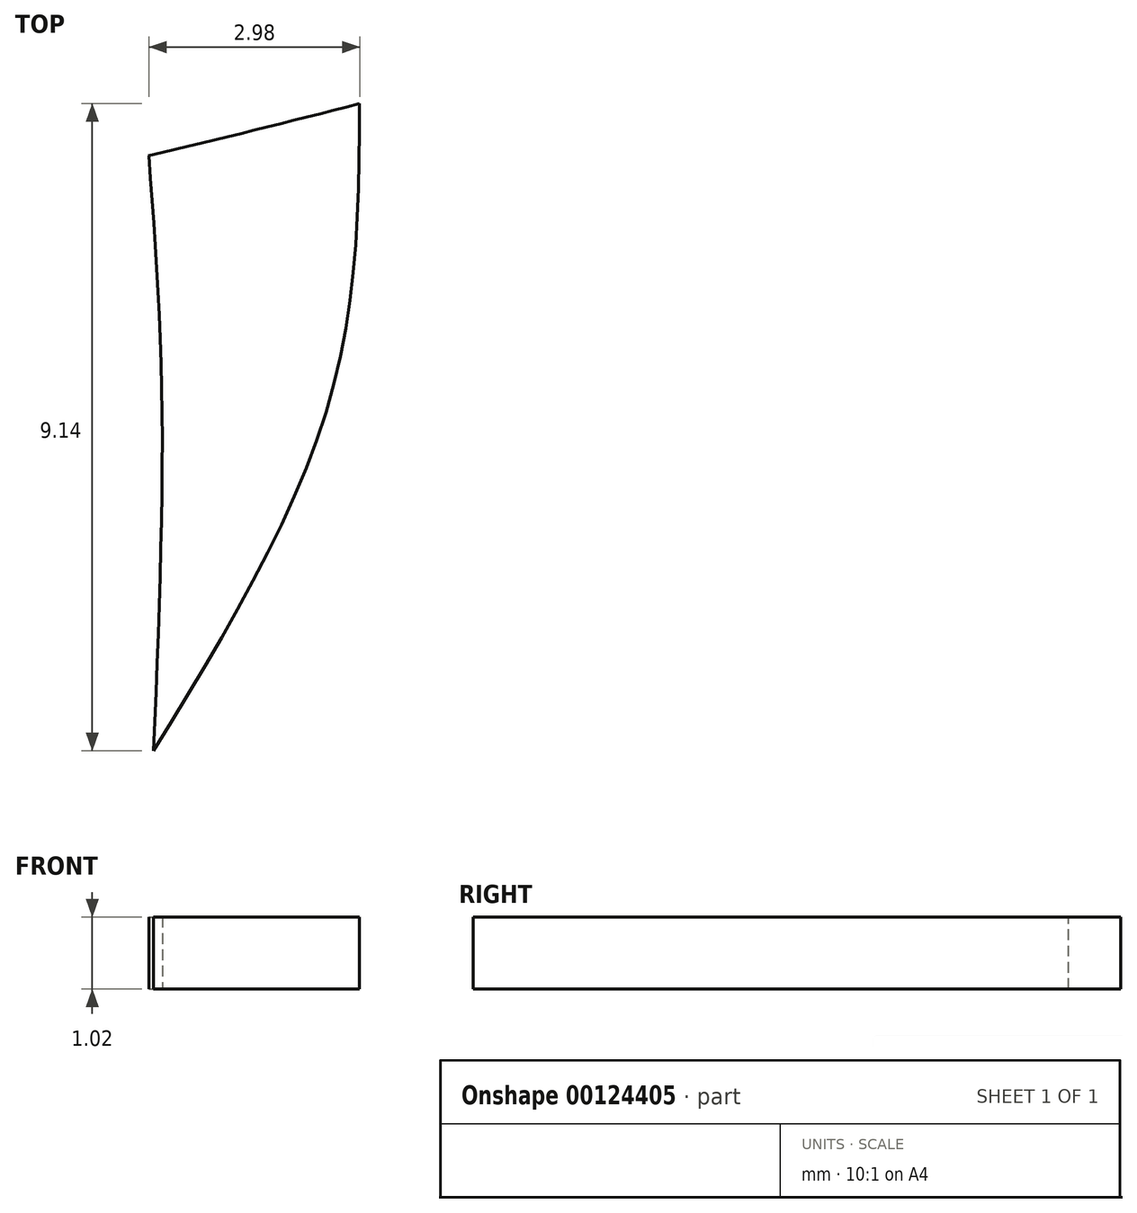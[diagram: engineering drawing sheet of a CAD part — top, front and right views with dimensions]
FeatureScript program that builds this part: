
annotation { "Feature Type Name" : "Feature", "Feature Type Description" : "" }
export const myFeature = defineFeature(function(context is Context, id is Id, definition is map)
    precondition{}
    {
        {
            var Q0;
            Q0=qCreatedBy(makeId("Top.planeOp"),FACE);
            var sketch = newSketch(context, id + "F0", { "sketchPlane" : qUnion([Q0])});
            skCircle(sketch, "E0", {"center": v(-65.84, 32.23) * mm, "radius": 0.65 * mm});
            skSolve(sketch);
        }
        {
            var Q0;
            Q0=qCreatedBy(makeId("Top.planeOp"),FACE);
            var sketch = newSketch(context, id + "F1", { "sketchPlane" : qUnion([Q0])});
            skLineSegment(sketch, "E1", {"start": v(-110.86, 15.85) * mm, "end": v(-22.98, 15.85) * mm});
            skLineSegment(sketch, "E2", {"start": v(-22.98, 15.85) * mm, "end": v(-22.98, -6.27) * mm});
            skLineSegment(sketch, "E3", {"start": v(-110.86, 15.85) * mm, "end": v(-110.86, -6.84) * mm});
            skArc(sketch, "E4", {"start": v(-110.86, -6.84) * mm, "mid": v(-66.88, -13.24) * mm, "end": v(-22.98, -6.27) * mm});
            skFitSpline(sketch, "E5", {"points": [v(-30.88, -8.55) * mm, v(-31.34, -12.85) * mm, v(-33.8, -17.7) * mm], "startDerivative": vector(-0.02, -9.29) * mm, "endDerivative": vector(-5.65, -9.2) * mm});
            skFitSpline(sketch, "E6", {"points": [v(-33.86, -9.29) * mm, v(-33.68, -12.73) * mm, v(-33.8, -17.7) * mm], "startDerivative": vector(0.57, -7.27) * mm, "endDerivative": vector(-0.39, -9.52) * mm});
            skLineSegment(sketch, "E7", {"start": v(-22.98, 15.85) * mm, "end": v(-99.18, 15.85) * mm});
            skLineSegment(sketch, "E8", {"start": v(-99.18, 15.85) * mm, "end": v(-99.18, -9.88) * mm});
            skSolve(sketch);
        }
        {
            var Q0;
            Q0=qCreatedBy(makeId("Top.planeOp"),FACE);
            var sketch = newSketch(context, id + "F2", { "sketchPlane" : qUnion([Q0])});
            skLineSegment(sketch, "E9.bottom", {"start": v(-59.53, 60.83) * mm, "end": v(15.65, 60.83) * mm});
            skLineSegment(sketch, "E9.top", {"start": v(-59.53, 26.54) * mm, "end": v(15.65, 26.54) * mm});
            skLineSegment(sketch, "E9.left", {"start": v(-59.53, 60.83) * mm, "end": v(-59.53, 26.54) * mm});
            skLineSegment(sketch, "E9.right", {"start": v(15.65, 60.83) * mm, "end": v(15.65, 26.54) * mm});
            skLineSegment(sketch, "E10.bottom", {"start": v(15.65, 26.54) * mm, "end": v(-12.7, 26.54) * mm});
            skLineSegment(sketch, "E10.top", {"start": v(15.65, 45.59) * mm, "end": v(-12.7, 45.59) * mm});
            skLineSegment(sketch, "E10.left", {"start": v(15.65, 26.54) * mm, "end": v(15.65, 45.59) * mm});
            skLineSegment(sketch, "E10.right", {"start": v(-12.7, 26.54) * mm, "end": v(-12.7, 45.59) * mm});
            skSolve(sketch);
        }
        {
            var Q0;
            Q0=makeQuery(id+"F1.imprint","IMPRINT",FACE,{"disambiguationData":[TD([[makeQuery(id+"F1.imprint","IMPRINT",EDGE,{"derivedFrom":sQuery(id+"F1.wireOp",EDGE,"7d530aef-c8df-49cc-a853-35ad8e8a77fe")}),1.0]])]});
            var Q1;
            Q1=makeQuery(id+"F1.imprint","IMPRINT",FACE,{"disambiguationData":[TD([[makeQuery(id+"F1.imprint","IMPRINT",EDGE,{"derivedFrom":sQuery(id+"F1.wireOp",EDGE,"2b311b18-58fd-43b0-ac47-cf94851b1c52")}),1.0]])]});
            var Q2;
            Q2=makeQuery(id+"F1.imprint","IMPRINT",FACE,{"disambiguationData":[TD([[makeQuery(id+"F1.imprint","IMPRINT",EDGE,{"derivedFrom":sQuery(id+"F1.wireOp",EDGE,"410c9de7-6207-49c7-be39-20c216db85bf")}),1.0]])]});
            var Q3;
            Q3=makeQuery(id+"F0.imprint","IMPRINT",FACE,{"disambiguationData":[TD([[makeQuery(id+"F0.imprint","IMPRINT",EDGE,{"derivedFrom":sQuery(id+"F0.wireOp",EDGE,"E0")}),1.0]])]});
            var Q4;
            Q4=makeQuery(id+"F1.imprint","IMPRINT",FACE,{"disambiguationData":[TD([[makeQuery(id+"F1.imprint","IMPRINT",EDGE,{"derivedFrom":sQuery(id+"F1.wireOp",EDGE,"8f773712-27e5-4475-b0bc-b5b0b1b0142c")}),1.0]])]});
            var Q5;
            Q5=makeQuery(id+"F1.imprint","IMPRINT",FACE,{"disambiguationData":[TD([[makeQuery(id+"F1.imprint","IMPRINT",EDGE,{"derivedFrom":sQuery(id+"F1.wireOp",EDGE,"cdf477c9-51f3-44c7-bcdf-c6a147e22681")}),1.0]])]});
            var Q6;
            Q6=makeQuery(id+"F1.imprint","IMPRINT",FACE,{"disambiguationData":[TD([[makeQuery(id+"F1.imprint","IMPRINT",EDGE,{"derivedFrom":sQuery(id+"F1.wireOp",EDGE,"8c1e2644-bb36-4412-ad06-52bd8adad983")}),1.0]])]});
            var Q7;
            Q7=makeQuery(id+"F1.imprint","IMPRINT",FACE,{"disambiguationData":[TD([[makeQuery(id+"F1.imprint","IMPRINT",EDGE,{"derivedFrom":sQuery(id+"F1.wireOp",EDGE,"afb39670-50f2-49b1-be07-c2a09c23c589")}),1.0]])]});
            var Q8;
            Q8=makeQuery(id+"F1.imprint","IMPRINT",FACE,{"disambiguationData":[TD([[makeQuery(id+"F1.imprint","IMPRINT",EDGE,{"derivedFrom":sQuery(id+"F1.wireOp",EDGE,"1c02878d-3e23-409d-a322-f7ee412d3750")}),1.0]])]});
            var Q9;
            Q9=makeQuery(id+"F1.imprint","IMPRINT",FACE,{"disambiguationData":[TD([[makeQuery(id+"F1.imprint","IMPRINT",EDGE,{"derivedFrom":sQuery(id+"F1.wireOp",EDGE,"2e7f4e81-c6df-418f-94df-d4b0b7ba906e")}),1.0]])]});
            var Q10;
            Q10=makeQuery(id+"F1.imprint","IMPRINT",FACE,{"disambiguationData":[TD([[makeQuery(id+"F1.imprint","IMPRINT",EDGE,{"derivedFrom":sQuery(id+"F1.wireOp",EDGE,"bfb1065a-cab9-4898-b917-bb85fffde635")}),1.0]])]});
            var Q11;
            Q11=makeQuery(id+"F1.imprint","IMPRINT",FACE,{"disambiguationData":[TD([[makeQuery(id+"F1.imprint","IMPRINT",EDGE,{"derivedFrom":sQuery(id+"F1.wireOp",EDGE,"21019b6d-9225-4829-b8bd-877c992cc65f")}),1.0]])]});
            var Q12;
            Q12=makeQuery(id+"F1.imprint","IMPRINT",FACE,{"disambiguationData":[TD([[makeQuery(id+"F1.imprint","IMPRINT",EDGE,{"derivedFrom":sQuery(id+"F1.wireOp",EDGE,"e37c8894-658f-4642-971c-f70e5ecd7af9")}),1.0]])]});
            var Q13;
            Q13=makeQuery(id+"F1.imprint","IMPRINT",FACE,{"disambiguationData":[TD([[makeQuery(id+"F1.imprint","IMPRINT",EDGE,{"derivedFrom":sQuery(id+"F1.wireOp",EDGE,"4e26d3ae-beb9-4c1a-93ba-002415f0acb0")}),1.0]])]});
            var Q14;
            Q14=makeQuery(id+"F1.imprint","IMPRINT",FACE,{"disambiguationData":[TD([[makeQuery(id+"F1.imprint","IMPRINT",EDGE,{"derivedFrom":sQuery(id+"F1.wireOp",EDGE,"84f1e03e-5a21-4721-94f0-bdbfdc29db09")}),1.0]])]});
            var Q15;
            Q15=makeQuery(id+"F1.imprint","IMPRINT",FACE,{"disambiguationData":[TD([[makeQuery(id+"F1.imprint","IMPRINT",EDGE,{"derivedFrom":sQuery(id+"F1.wireOp",EDGE,"25d9cc1b-062b-4bb5-9ce4-53bc4fe40080")}),1.0]])]});
            var Q16;
            Q16=makeQuery(id+"F1.imprint","IMPRINT",FACE,{"disambiguationData":[TD([[makeQuery(id+"F1.imprint","IMPRINT",EDGE,{"derivedFrom":sQuery(id+"F1.wireOp",EDGE,"fc0269ad-6765-42d2-a3f1-cf348a22c25d")}),1.0]])]});
            var Q17;
            Q17=makeQuery(id+"F1.imprint","IMPRINT",FACE,{"disambiguationData":[TD([[makeQuery(id+"F1.imprint","IMPRINT",EDGE,{"derivedFrom":sQuery(id+"F1.wireOp",EDGE,"187869be-c3a0-4a53-b3f3-32ef39bbe492")}),1.0]])]});
            var Q18;
            Q18=makeQuery(id+"F1.imprint","IMPRINT",FACE,{"disambiguationData":[TD([[makeQuery(id+"F1.imprint","IMPRINT",EDGE,{"derivedFrom":sQuery(id+"F1.wireOp",EDGE,"9fa9e04d-5760-4a40-aeb6-4168d89a4eef")}),1.0]])]});
            var Q19;
            Q19=makeQuery(id+"F1.imprint","IMPRINT",FACE,{"disambiguationData":[TD([[makeQuery(id+"F1.imprint","IMPRINT",EDGE,{"derivedFrom":sQuery(id+"F1.wireOp",EDGE,"c71889e1-eb4f-436c-9950-13deb293f1db")}),1.0]])]});
            var Q20;
            Q20=makeQuery(id+"F1.imprint","IMPRINT",FACE,{"disambiguationData":[TD([[makeQuery(id+"F1.imprint","IMPRINT",EDGE,{"derivedFrom":sQuery(id+"F1.wireOp",EDGE,"afdb87ec-d79a-45a9-a05c-717156bfb7cd")}),1.0]])]});
            var Q21;
            Q21=makeQuery(id+"F1.imprint","IMPRINT",FACE,{"disambiguationData":[TD([[makeQuery(id+"F1.imprint","IMPRINT",EDGE,{"derivedFrom":sQuery(id+"F1.wireOp",EDGE,"a48a8bff-ce23-473c-b1c0-9448eced9b32")}),1.0]])]});
            var Q22;
            Q22=makeQuery(id+"F1.imprint","IMPRINT",FACE,{"disambiguationData":[TD([[makeQuery(id+"F1.imprint","IMPRINT",EDGE,{"derivedFrom":sQuery(id+"F1.wireOp",EDGE,"8f9b4e0b-b456-4ce4-89e9-5843fb71aecc")}),1.0]])]});
            var Q23;
            Q23=makeQuery(id+"F1.imprint","IMPRINT",FACE,{"disambiguationData":[TD([[makeQuery(id+"F1.imprint","IMPRINT",EDGE,{"derivedFrom":sQuery(id+"F1.wireOp",EDGE,"d69b603a-0a3a-470c-87fb-5fe536fbcdfb")}),1.0]])]});
            var Q24;
            Q24=makeQuery(id+"F1.imprint","IMPRINT",FACE,{"disambiguationData":[TD([[makeQuery(id+"F1.imprint","IMPRINT",EDGE,{"derivedFrom":sQuery(id+"F1.wireOp",EDGE,"48f5f1cd-c210-4d07-9456-369a695a64fd")}),1.0]])]});
            var Q25;
            Q25=makeQuery(id+"F1.imprint","IMPRINT",FACE,{"disambiguationData":[TD([[makeQuery(id+"F1.imprint","IMPRINT",EDGE,{"derivedFrom":sQuery(id+"F1.wireOp",EDGE,"05a9797e-15e3-4fd6-a2da-66079b940148")}),1.0]])]});
            var Q26;
            Q26=makeQuery(id+"F1.imprint","IMPRINT",FACE,{"disambiguationData":[TD([[makeQuery(id+"F1.imprint","IMPRINT",EDGE,{"derivedFrom":sQuery(id+"F1.wireOp",EDGE,"ce97bbf4-a538-4860-89d0-490cc9d6ba0e")}),1.0]])]});
            var Q27;
            Q27=makeQuery(id+"F1.imprint","IMPRINT",FACE,{"disambiguationData":[TD([[makeQuery(id+"F1.imprint","IMPRINT",EDGE,{"derivedFrom":sQuery(id+"F1.wireOp",EDGE,"5fa7571f-411c-4993-86c9-208f069f7377")}),1.0]])]});
            var Q28;
            Q28=makeQuery(id+"F1.imprint","IMPRINT",FACE,{"disambiguationData":[TD([[makeQuery(id+"F1.imprint","IMPRINT",EDGE,{"derivedFrom":sQuery(id+"F1.wireOp",EDGE,"1b0e43d8-f7af-48e3-ac0b-2aa93e71bc35")}),1.0]])]});
            var Q29;
            Q29=makeQuery(id+"F1.imprint","IMPRINT",FACE,{"disambiguationData":[TD([[makeQuery(id+"F1.imprint","IMPRINT",EDGE,{"derivedFrom":sQuery(id+"F1.wireOp",EDGE,"47c9dda0-eb43-4ddc-b7b5-d2f01c861544")}),1.0]])]});
            var Q30;
            Q30=makeQuery(id+"F1.imprint","IMPRINT",FACE,{"disambiguationData":[TD([[makeQuery(id+"F1.imprint","IMPRINT",EDGE,{"derivedFrom":sQuery(id+"F1.wireOp",EDGE,"3b40a63c-9782-4902-8a86-c3139b9eb764")}),1.0]])]});
            var Q31;
            Q31=makeQuery(id+"F1.imprint","IMPRINT",FACE,{"disambiguationData":[TD([[makeQuery(id+"F1.imprint","IMPRINT",EDGE,{"derivedFrom":sQuery(id+"F1.wireOp",EDGE,"6d958931-b70a-49d3-b1e5-2076e474eeb5")}),1.0]])]});
            var Q32;
            Q32=makeQuery(id+"F1.imprint","IMPRINT",FACE,{"disambiguationData":[TD([[makeQuery(id+"F1.imprint","IMPRINT",EDGE,{"derivedFrom":sQuery(id+"F1.wireOp",EDGE,"b4ff40dc-20b4-4bd3-89fc-f102a9961f8c")}),1.0]])]});
            var Q33;
            Q33=makeQuery(id+"F1.imprint","IMPRINT",FACE,{"disambiguationData":[TD([[makeQuery(id+"F1.imprint","IMPRINT",EDGE,{"derivedFrom":sQuery(id+"F1.wireOp",EDGE,"b71d4cb1-866b-4d81-a721-a0ad96be9b8b")}),1.0]])]});
            var Q34;
            Q34=makeQuery(id+"F1.imprint","IMPRINT",FACE,{"disambiguationData":[TD([[makeQuery(id+"F1.imprint","IMPRINT",EDGE,{"derivedFrom":sQuery(id+"F1.wireOp",EDGE,"f7c1084b-d84e-4c82-aa00-e076926db26a")}),1.0]])]});
            var Q35;
            Q35=makeQuery(id+"F1.imprint","IMPRINT",FACE,{"disambiguationData":[TD([[makeQuery(id+"F1.imprint","IMPRINT",EDGE,{"derivedFrom":sQuery(id+"F1.wireOp",EDGE,"a09209f8-7044-4cf4-8aec-d30c1fa2ae95")}),1.0]])]});
            var Q36;
            Q36=makeQuery(id+"F1.imprint","IMPRINT",FACE,{"disambiguationData":[TD([[makeQuery(id+"F1.imprint","IMPRINT",EDGE,{"derivedFrom":sQuery(id+"F1.wireOp",EDGE,"484d747a-906d-4482-9977-9e7a5c9f7520")}),1.0]])]});
            var Q37;
            Q37=makeQuery(id+"F1.imprint","IMPRINT",FACE,{"disambiguationData":[TD([[makeQuery(id+"F1.imprint","IMPRINT",EDGE,{"derivedFrom":sQuery(id+"F1.wireOp",EDGE,"55a967fc-cf59-4a71-bfac-7d7444c0d945")}),1.0]])]});
            var Q38;
            Q38=makeQuery(id+"F1.imprint","IMPRINT",FACE,{"disambiguationData":[TD([[makeQuery(id+"F1.imprint","IMPRINT",EDGE,{"derivedFrom":sQuery(id+"F1.wireOp",EDGE,"9d3ff30b-5d5f-465d-aec8-0f0612a3a9cd")}),1.0]])]});
            var Q39;
            Q39=makeQuery(id+"F1.imprint","IMPRINT",FACE,{"disambiguationData":[TD([[makeQuery(id+"F1.imprint","IMPRINT",EDGE,{"derivedFrom":sQuery(id+"F1.wireOp",EDGE,"e43c900f-e10d-4cac-8d11-2e5689b6b1d5")}),1.0]])]});
            var Q40;
            Q40=makeQuery(id+"F1.imprint","IMPRINT",FACE,{"disambiguationData":[TD([[makeQuery(id+"F1.imprint","IMPRINT",EDGE,{"derivedFrom":sQuery(id+"F1.wireOp",EDGE,"a9e5a808-2ef5-4392-9576-852277e467f2")}),1.0]])]});
            var Q41;
            Q41=makeQuery(id+"F1.imprint","IMPRINT",FACE,{"disambiguationData":[TD([[makeQuery(id+"F1.imprint","IMPRINT",EDGE,{"derivedFrom":sQuery(id+"F1.wireOp",EDGE,"56acc55b-9546-466a-93d2-c752bbd7866e")}),1.0]])]});
            var Q42;
            Q42=makeQuery(id+"F1.imprint","IMPRINT",FACE,{"disambiguationData":[TD([[makeQuery(id+"F1.imprint","IMPRINT",EDGE,{"derivedFrom":sQuery(id+"F1.wireOp",EDGE,"20040cfe-7ec2-40a3-b60c-debe91aca25c")}),1.0]])]});
            var Q43;
            Q43=makeQuery(id+"F1.imprint","IMPRINT",FACE,{"disambiguationData":[TD([[makeQuery(id+"F1.imprint","IMPRINT",EDGE,{"derivedFrom":sQuery(id+"F1.wireOp",EDGE,"7d899a2b-71f5-44ce-8364-893d38b0a961")}),1.0]])]});
            var Q44;
            Q44=makeQuery(id+"F1.imprint","IMPRINT",FACE,{"disambiguationData":[TD([[makeQuery(id+"F1.imprint","IMPRINT",EDGE,{"derivedFrom":sQuery(id+"F1.wireOp",EDGE,"559fe54c-6345-47de-806c-53990a12e350")}),1.0]])]});
            var Q45;
            Q45=makeQuery(id+"F1.imprint","IMPRINT",FACE,{"disambiguationData":[TD([[makeQuery(id+"F1.imprint","IMPRINT",EDGE,{"derivedFrom":sQuery(id+"F1.wireOp",EDGE,"4b321e91-a8a1-4189-b260-94da62a27512")}),1.0]])]});
            var Q46;
            Q46=makeQuery(id+"F1.imprint","IMPRINT",FACE,{"disambiguationData":[TD([[makeQuery(id+"F1.imprint","IMPRINT",EDGE,{"derivedFrom":sQuery(id+"F1.wireOp",EDGE,"dc40b896-e991-42b1-9757-3a5ebb1f78ea")}),1.0]])]});
            var Q47;
            Q47=makeQuery(id+"F1.imprint","IMPRINT",FACE,{"disambiguationData":[TD([[makeQuery(id+"F1.imprint","IMPRINT",EDGE,{"derivedFrom":sQuery(id+"F1.wireOp",EDGE,"85043f60-7fef-43b8-ba61-ac2b7be8fe33")}),1.0]])]});
            var Q48;
            Q48=makeQuery(id+"F1.imprint","IMPRINT",FACE,{"disambiguationData":[TD([[makeQuery(id+"F1.imprint","IMPRINT",EDGE,{"derivedFrom":sQuery(id+"F1.wireOp",EDGE,"39267c74-a86e-4a0a-b377-4f9ec4585843")}),1.0]])]});
            var Q49;
            Q49=makeQuery(id+"F1.imprint","IMPRINT",FACE,{"disambiguationData":[TD([[makeQuery(id+"F1.imprint","IMPRINT",EDGE,{"derivedFrom":sQuery(id+"F1.wireOp",EDGE,"40bdc2a5-2341-4f5c-a56b-06b630dfa9fc")}),1.0]])]});
            var Q50;
            Q50=makeQuery(id+"F1.imprint","IMPRINT",FACE,{"disambiguationData":[TD([[makeQuery(id+"F1.imprint","IMPRINT",EDGE,{"derivedFrom":sQuery(id+"F1.wireOp",EDGE,"1916121b-87e3-42fd-bb47-9bf82f42e5d9")}),1.0]])]});
            var Q51;
            Q51=makeQuery(id+"F1.imprint","IMPRINT",FACE,{"disambiguationData":[TD([[makeQuery(id+"F1.imprint","IMPRINT",EDGE,{"derivedFrom":sQuery(id+"F1.wireOp",EDGE,"c8bbaf4e-987e-4e69-8a47-3c79a83e0c87")}),1.0]])]});
            var Q52;
            Q52=makeQuery(id+"F1.imprint","IMPRINT",FACE,{"disambiguationData":[TD([[makeQuery(id+"F1.imprint","IMPRINT",EDGE,{"derivedFrom":sQuery(id+"F1.wireOp",EDGE,"3106ccec-705c-4960-a74f-be933f157d40")}),1.0]])]});
            var Q53;
            Q53=makeQuery(id+"F1.imprint","IMPRINT",FACE,{"disambiguationData":[TD([[makeQuery(id+"F1.imprint","IMPRINT",EDGE,{"derivedFrom":sQuery(id+"F1.wireOp",EDGE,"407f0a36-e44a-4196-afc8-af34e5d263da")}),1.0]])]});
            var Q54;
            Q54=makeQuery(id+"F1.imprint","IMPRINT",FACE,{"disambiguationData":[TD([[makeQuery(id+"F1.imprint","IMPRINT",EDGE,{"derivedFrom":sQuery(id+"F1.wireOp",EDGE,"7cfd9803-ecd4-4c70-86c0-bd39d4e26022")}),1.0]])]});
            var Q55;
            Q55=makeQuery(id+"F1.imprint","IMPRINT",FACE,{"disambiguationData":[TD([[makeQuery(id+"F1.imprint","IMPRINT",EDGE,{"derivedFrom":sQuery(id+"F1.wireOp",EDGE,"7924a3fe-2feb-48c6-84bb-4c5bd13528d8")}),1.0]])]});
            var Q56;
            Q56=makeQuery(id+"F1.imprint","IMPRINT",FACE,{"disambiguationData":[TD([[makeQuery(id+"F1.imprint","IMPRINT",EDGE,{"derivedFrom":sQuery(id+"F1.wireOp",EDGE,"3b7f7286-30fc-4e50-92d2-53d9abb117fb")}),1.0]])]});
            var Q57;
            Q57=makeQuery(id+"F1.imprint","IMPRINT",FACE,{"disambiguationData":[TD([[makeQuery(id+"F1.imprint","IMPRINT",EDGE,{"derivedFrom":sQuery(id+"F1.wireOp",EDGE,"4a20ea9f-2355-40fc-b659-074ddab8549f")}),1.0]])]});
            var Q58;
            Q58=makeQuery(id+"F1.imprint","IMPRINT",FACE,{"disambiguationData":[TD([[makeQuery(id+"F1.imprint","IMPRINT",EDGE,{"derivedFrom":sQuery(id+"F1.wireOp",EDGE,"53b61e4c-e748-4765-b0b8-36f6e8858f6d")}),1.0]])]});
            var Q59;
            Q59=makeQuery(id+"F1.imprint","IMPRINT",FACE,{"disambiguationData":[TD([[makeQuery(id+"F1.imprint","IMPRINT",EDGE,{"derivedFrom":sQuery(id+"F1.wireOp",EDGE,"25661483-70bc-4f2a-a87d-232d989049ff")}),1.0]])]});
            var Q60;
            Q60=makeQuery(id+"F1.imprint","IMPRINT",FACE,{"disambiguationData":[TD([[makeQuery(id+"F1.imprint","IMPRINT",EDGE,{"derivedFrom":sQuery(id+"F1.wireOp",EDGE,"ddde8b18-6fe0-4bc3-820a-1cbee6d39207")}),1.0]])]});
            var Q61;
            Q61=makeQuery(id+"F1.imprint","IMPRINT",FACE,{"disambiguationData":[TD([[makeQuery(id+"F1.imprint","IMPRINT",EDGE,{"derivedFrom":sQuery(id+"F1.wireOp",EDGE,"0a267213-7c40-419e-a7d2-6af8714e5f45")}),1.0]])]});
            var Q62;
            Q62=makeQuery(id+"F1.imprint","IMPRINT",FACE,{"disambiguationData":[TD([[makeQuery(id+"F1.imprint","IMPRINT",EDGE,{"derivedFrom":sQuery(id+"F1.wireOp",EDGE,"ba64a743-74b2-49ca-b953-3069a09bc900")}),1.0]])]});
            var Q63;
            Q63=makeQuery(id+"F1.imprint","IMPRINT",FACE,{"disambiguationData":[TD([[makeQuery(id+"F1.imprint","IMPRINT",EDGE,{"derivedFrom":sQuery(id+"F1.wireOp",EDGE,"946e2664-ac89-45e9-bb45-cd7e8761c812")}),1.0]])]});
            var Q64;
            Q64=makeQuery(id+"F1.imprint","IMPRINT",FACE,{"disambiguationData":[TD([[makeQuery(id+"F1.imprint","IMPRINT",EDGE,{"derivedFrom":sQuery(id+"F1.wireOp",EDGE,"351b4d51-b6fd-40e4-8a24-322787a033b8")}),1.0]])]});
            var Q65;
            Q65=makeQuery(id+"F1.imprint","IMPRINT",FACE,{"disambiguationData":[TD([[makeQuery(id+"F1.imprint","IMPRINT",EDGE,{"derivedFrom":sQuery(id+"F1.wireOp",EDGE,"b0e0dee2-7c40-486c-a8eb-da6d1aebb478")}),1.0]])]});
            var Q66;
            Q66=makeQuery(id+"F1.imprint","IMPRINT",FACE,{"disambiguationData":[TD([[makeQuery(id+"F1.imprint","IMPRINT",EDGE,{"derivedFrom":sQuery(id+"F1.wireOp",EDGE,"80e09545-e805-4756-afb3-e908e0697b95")}),1.0]])]});
            var Q67;
            Q67=makeQuery(id+"F1.imprint","IMPRINT",FACE,{"disambiguationData":[TD([[makeQuery(id+"F1.imprint","IMPRINT",EDGE,{"derivedFrom":sQuery(id+"F1.wireOp",EDGE,"04816a61-eb0e-4346-90f7-c6d7124d8b43")}),1.0]])]});
            var Q68;
            Q68=makeQuery(id+"F1.imprint","IMPRINT",FACE,{"disambiguationData":[TD([[makeQuery(id+"F1.imprint","IMPRINT",EDGE,{"derivedFrom":sQuery(id+"F1.wireOp",EDGE,"6f771d5e-fdfe-4922-8dcd-cc699ffee86c")}),1.0]])]});
            var Q69;
            Q69=makeQuery(id+"F1.imprint","IMPRINT",FACE,{"disambiguationData":[TD([[makeQuery(id+"F1.imprint","IMPRINT",EDGE,{"derivedFrom":sQuery(id+"F1.wireOp",EDGE,"7079bfff-28f3-4683-ae2e-cec7d5cb01cb")}),1.0]])]});
            var Q70;
            Q70=makeQuery(id+"F1.imprint","IMPRINT",FACE,{"disambiguationData":[TD([[makeQuery(id+"F1.imprint","IMPRINT",EDGE,{"derivedFrom":sQuery(id+"F1.wireOp",EDGE,"IQYQTx4D-fJSk-LKtq-i42c-D6EXXIsjCsXz")}),1.0]])]});
            var Q71;
            Q71=makeQuery(id+"F1.imprint","IMPRINT",FACE,{"disambiguationData":[TD([[makeQuery(id+"F1.imprint","IMPRINT",EDGE,{"derivedFrom":sQuery(id+"F1.wireOp",EDGE,"126f70df-1a0d-451e-9d83-f86c9f88abc8")}),1.0]])]});
            var Q72;
            Q72=makeQuery(id+"F1.imprint","IMPRINT",FACE,{"disambiguationData":[TD([[makeQuery(id+"F1.imprint","IMPRINT",EDGE,{"derivedFrom":sQuery(id+"F1.wireOp",EDGE,"e3f8fca8-a1ae-4d0b-93d8-ef3dc832972e")}),1.0]])]});
            var Q73;
            Q73=makeQuery(id+"F1.imprint","IMPRINT",FACE,{"disambiguationData":[TD([[makeQuery(id+"F1.imprint","IMPRINT",EDGE,{"derivedFrom":sQuery(id+"F1.wireOp",EDGE,"9eaee011-cf2f-4949-90a7-00d6302f023d")}),1.0]])]});
            var Q74;
            Q74=makeQuery(id+"F1.imprint","IMPRINT",FACE,{"disambiguationData":[TD([[makeQuery(id+"F1.imprint","IMPRINT",EDGE,{"derivedFrom":sQuery(id+"F1.wireOp",EDGE,"55cb77bc-91cc-4325-939e-488937f48d64")}),1.0]])]});
            var Q75;
            Q75=makeQuery(id+"F1.imprint","IMPRINT",FACE,{"disambiguationData":[TD([[makeQuery(id+"F1.imprint","IMPRINT",EDGE,{"derivedFrom":sQuery(id+"F1.wireOp",EDGE,"5ca0945c-6bbc-48af-a93b-5625915023c8")}),1.0]])]});
            var Q76;
            Q76=makeQuery(id+"F1.imprint","IMPRINT",FACE,{"disambiguationData":[TD([[makeQuery(id+"F1.imprint","IMPRINT",EDGE,{"derivedFrom":sQuery(id+"F1.wireOp",EDGE,"bff61fca-36fd-4415-8d85-04465080573f")}),1.0]])]});
            var Q77;
            Q77=makeQuery(id+"F1.imprint","IMPRINT",FACE,{"disambiguationData":[TD([[makeQuery(id+"F1.imprint","IMPRINT",EDGE,{"derivedFrom":sQuery(id+"F1.wireOp",EDGE,"50d7f0cc-a3bc-44f1-927f-4ccd5fb9444e")}),1.0]])]});
            var Q78;
            Q78=makeQuery(id+"F1.imprint","IMPRINT",FACE,{"disambiguationData":[TD([[makeQuery(id+"F1.imprint","IMPRINT",EDGE,{"derivedFrom":sQuery(id+"F1.wireOp",EDGE,"ab028f4d-2498-446a-b172-ba7fe3d4d79f")}),1.0]])]});
            var Q79;
            Q79=makeQuery(id+"F1.imprint","IMPRINT",FACE,{"disambiguationData":[TD([[makeQuery(id+"F1.imprint","IMPRINT",EDGE,{"derivedFrom":sQuery(id+"F1.wireOp",EDGE,"61445ce6-51c2-4ac1-9eed-13ce467cc58e")}),1.0]])]});
            var Q80;
            Q80=makeQuery(id+"F1.imprint","IMPRINT",FACE,{"disambiguationData":[TD([[makeQuery(id+"F1.imprint","IMPRINT",EDGE,{"derivedFrom":sQuery(id+"F1.wireOp",EDGE,"13c5ac6e-9f7b-46d0-b330-e33b265c37d4")}),1.0]])]});
            var Q81;
            Q81=makeQuery(id+"F1.imprint","IMPRINT",FACE,{"disambiguationData":[TD([[makeQuery(id+"F1.imprint","IMPRINT",EDGE,{"derivedFrom":sQuery(id+"F1.wireOp",EDGE,"e07ccc40-30e0-4116-87f5-dd35409532ab")}),1.0]])]});
            var Q82;
            Q82=makeQuery(id+"F1.imprint","IMPRINT",FACE,{"disambiguationData":[TD([[makeQuery(id+"F1.imprint","IMPRINT",EDGE,{"derivedFrom":sQuery(id+"F1.wireOp",EDGE,"d94de641-2fb7-41d4-b6e0-2e3dc5f59612")}),1.0]])]});
            var Q83;
            Q83=makeQuery(id+"F1.imprint","IMPRINT",FACE,{"disambiguationData":[TD([[makeQuery(id+"F1.imprint","IMPRINT",EDGE,{"derivedFrom":sQuery(id+"F1.wireOp",EDGE,"bc114b7d-a9ae-4e2b-965a-efcba974dd4e")}),1.0]])]});
            var Q84;
            Q84=makeQuery(id+"F1.imprint","IMPRINT",FACE,{"disambiguationData":[TD([[makeQuery(id+"F1.imprint","IMPRINT",EDGE,{"derivedFrom":sQuery(id+"F1.wireOp",EDGE,"6e8f4bdd-71aa-42b2-a188-63b31c486d87")}),1.0]])]});
            var Q85;
            Q85=makeQuery(id+"F1.imprint","IMPRINT",FACE,{"disambiguationData":[TD([[makeQuery(id+"F1.imprint","IMPRINT",EDGE,{"derivedFrom":sQuery(id+"F1.wireOp",EDGE,"0e15a808-7b14-42e8-9234-6df6935beb3e")}),1.0]])]});
            var Q86;
            Q86=makeQuery(id+"F1.imprint","IMPRINT",FACE,{"disambiguationData":[TD([[makeQuery(id+"F1.imprint","IMPRINT",EDGE,{"derivedFrom":sQuery(id+"F1.wireOp",EDGE,"25866dd3-af03-4969-bc58-9b283e6d481b")}),1.0]])]});
            var Q87;
            Q87=makeQuery(id+"F1.imprint","IMPRINT",FACE,{"disambiguationData":[TD([[makeQuery(id+"F1.imprint","IMPRINT",EDGE,{"derivedFrom":sQuery(id+"F1.wireOp",EDGE,"7f88ff2e-a912-4057-b699-7ce09ea38530")}),1.0]])]});
            var Q88;
            Q88=makeQuery(id+"F1.imprint","IMPRINT",FACE,{"disambiguationData":[TD([[makeQuery(id+"F1.imprint","IMPRINT",EDGE,{"derivedFrom":sQuery(id+"F1.wireOp",EDGE,"d3ae8674-74f6-49cf-8c5c-0de1270b44e5")}),1.0]])]});
            var Q89;
            Q89=makeQuery(id+"F1.imprint","IMPRINT",FACE,{"disambiguationData":[TD([[makeQuery(id+"F1.imprint","IMPRINT",EDGE,{"derivedFrom":sQuery(id+"F1.wireOp",EDGE,"c751a891-51ce-4e8d-9e0e-479f614fe617")}),1.0]])]});
            var Q90;
            Q90=makeQuery(id+"F1.imprint","IMPRINT",FACE,{"disambiguationData":[TD([[makeQuery(id+"F1.imprint","IMPRINT",EDGE,{"derivedFrom":sQuery(id+"F1.wireOp",EDGE,"f6faf651-b7ee-4778-ad8d-2e4a8e9642f7")}),1.0]])]});
            var Q91;
            Q91=makeQuery(id+"F1.imprint","IMPRINT",FACE,{"disambiguationData":[TD([[makeQuery(id+"F1.imprint","IMPRINT",EDGE,{"derivedFrom":sQuery(id+"F1.wireOp",EDGE,"a1965818-b970-4097-b521-540a1cb1f767")}),1.0]])]});
            var Q92;
            Q92=makeQuery(id+"F1.imprint","IMPRINT",FACE,{"disambiguationData":[TD([[makeQuery(id+"F1.imprint","IMPRINT",EDGE,{"derivedFrom":sQuery(id+"F1.wireOp",EDGE,"7edd777e-64e0-4db0-8f52-2228dfb33078")}),1.0]])]});
            var Q93;
            Q93=makeQuery(id+"F1.imprint","IMPRINT",FACE,{"disambiguationData":[TD([[makeQuery(id+"F1.imprint","IMPRINT",EDGE,{"derivedFrom":sQuery(id+"F1.wireOp",EDGE,"150f6f36-60db-42e5-89f4-495b7c08a796")}),1.0]])]});
            var Q94;
            Q94=makeQuery(id+"F1.imprint","IMPRINT",FACE,{"disambiguationData":[TD([[makeQuery(id+"F1.imprint","IMPRINT",EDGE,{"derivedFrom":sQuery(id+"F1.wireOp",EDGE,"2cd982d5-0089-4635-972d-67435d39a214")}),1.0]])]});
            var Q95;
            Q95=makeQuery(id+"F1.imprint","IMPRINT",FACE,{"disambiguationData":[TD([[makeQuery(id+"F1.imprint","IMPRINT",EDGE,{"derivedFrom":sQuery(id+"F1.wireOp",EDGE,"2c68a5cc-583a-4e21-8d00-f2716ba61d92")}),1.0]])]});
            var Q96;
            Q96=makeQuery(id+"F1.imprint","IMPRINT",FACE,{"disambiguationData":[TD([[makeQuery(id+"F1.imprint","IMPRINT",EDGE,{"derivedFrom":sQuery(id+"F1.wireOp",EDGE,"5996a8f3-71d1-45d0-9633-99fc3c2019b6")}),1.0]])]});
            var Q97;
            Q97=makeQuery(id+"F1.imprint","IMPRINT",FACE,{"disambiguationData":[TD([[makeQuery(id+"F1.imprint","IMPRINT",EDGE,{"derivedFrom":sQuery(id+"F1.wireOp",EDGE,"2ee18cf7-4fb7-4b61-a3cf-e68d8f2852b4")}),1.0]])]});
            var Q98;
            Q98=makeQuery(id+"F1.imprint","IMPRINT",FACE,{"disambiguationData":[TD([[makeQuery(id+"F1.imprint","IMPRINT",EDGE,{"derivedFrom":sQuery(id+"F1.wireOp",EDGE,"5295e683-5c6e-4e8e-bbfe-81816525bda0")}),1.0]])]});
            var Q99;
            Q99=makeQuery(id+"F1.imprint","IMPRINT",FACE,{"disambiguationData":[TD([[makeQuery(id+"F1.imprint","IMPRINT",EDGE,{"derivedFrom":sQuery(id+"F1.wireOp",EDGE,"a645aaaa-f54e-411b-9215-a7927be1f780")}),1.0]])]});
            var Q100;
            Q100=makeQuery(id+"F1.imprint","IMPRINT",FACE,{"disambiguationData":[TD([[makeQuery(id+"F1.imprint","IMPRINT",EDGE,{"derivedFrom":sQuery(id+"F1.wireOp",EDGE,"0434efe0-d554-483d-bd28-34a7d8d0b50f")}),1.0]])]});
            var Q101;
            Q101=makeQuery(id+"F1.imprint","IMPRINT",FACE,{"disambiguationData":[TD([[makeQuery(id+"F1.imprint","IMPRINT",EDGE,{"derivedFrom":sQuery(id+"F1.wireOp",EDGE,"606e4ff4-c372-45cb-a36b-f10931f5497d")}),1.0]])]});
            var Q102;
            Q102=makeQuery(id+"F1.imprint","IMPRINT",FACE,{"disambiguationData":[TD([[makeQuery(id+"F1.imprint","IMPRINT",EDGE,{"derivedFrom":sQuery(id+"F1.wireOp",EDGE,"f4cf1d7a-71f4-429e-a2cf-aa9f5c4bf02f")}),1.0]])]});
            var Q103;
            Q103=makeQuery(id+"F1.imprint","IMPRINT",FACE,{"disambiguationData":[TD([[makeQuery(id+"F1.imprint","IMPRINT",EDGE,{"derivedFrom":sQuery(id+"F1.wireOp",EDGE,"722cfd06-0ee1-456e-8828-1f596be15dbe")}),1.0]])]});
            var Q104;
            Q104=makeQuery(id+"F1.imprint","IMPRINT",FACE,{"disambiguationData":[TD([[makeQuery(id+"F1.imprint","IMPRINT",EDGE,{"derivedFrom":sQuery(id+"F1.wireOp",EDGE,"19382886-88d1-4d62-8e9d-aeeddef3f290")}),1.0]])]});
            var Q105;
            Q105=makeQuery(id+"F1.imprint","IMPRINT",FACE,{"disambiguationData":[TD([[makeQuery(id+"F1.imprint","IMPRINT",EDGE,{"derivedFrom":sQuery(id+"F1.wireOp",EDGE,"1a7c10c3-2d57-4d46-a384-873822354761")}),1.0]])]});
            var Q106;
            Q106=makeQuery(id+"F1.imprint","IMPRINT",FACE,{"disambiguationData":[TD([[makeQuery(id+"F1.imprint","IMPRINT",EDGE,{"derivedFrom":sQuery(id+"F1.wireOp",EDGE,"9dde0bd0-4224-40f4-94b5-97fa1c3db23d")}),1.0]])]});
            var Q107;
            Q107=makeQuery(id+"F1.imprint","IMPRINT",FACE,{"disambiguationData":[TD([[makeQuery(id+"F1.imprint","IMPRINT",EDGE,{"derivedFrom":sQuery(id+"F1.wireOp",EDGE,"5daa7517-ec5d-4592-a1ac-977ff9070edf")}),1.0]])]});
            var Q108;
            Q108=makeQuery(id+"F1.imprint","IMPRINT",FACE,{"disambiguationData":[TD([[makeQuery(id+"F1.imprint","IMPRINT",EDGE,{"derivedFrom":sQuery(id+"F1.wireOp",EDGE,"d1da2f99-7152-417c-86a7-0e482ec30a58")}),1.0]])]});
            var Q109;
            Q109=makeQuery(id+"F1.imprint","IMPRINT",FACE,{"disambiguationData":[TD([[makeQuery(id+"F1.imprint","IMPRINT",EDGE,{"derivedFrom":sQuery(id+"F1.wireOp",EDGE,"95b728b6-ea23-49c0-ab31-382de2099b98")}),1.0]])]});
            extrude(context, id + "F3", {"entities" : qUnion([Q0, Q1, Q2, Q3, Q4, Q5, Q6, Q7, Q8, Q9, Q10, Q11, Q12, Q13, Q14, Q15, Q16, Q17, Q18, Q19, Q20, Q21, Q22, Q23, Q24, Q25, Q26, Q27, Q28, Q29, Q30, Q31, Q32, Q33, Q34, Q35, Q36, Q37, Q38, Q39, Q40, Q41, Q42, Q43, Q44, Q45, Q46, Q47, Q48, Q49, Q50, Q51, Q52, Q53, Q54, Q55, Q56, Q57, Q58, Q59, Q60, Q61, Q62, Q63, Q64, Q65, Q66, Q67, Q68, Q69, Q70, Q71, Q72, Q73, Q74, Q75, Q76, Q77, Q78, Q79, Q80, Q81, Q82, Q83, Q84, Q85, Q86, Q87, Q88, Q89, Q90, Q91, Q92, Q93, Q94, Q95, Q96, Q97, Q98, Q99, Q100, Q101, Q102, Q103, Q104, Q105, Q106, Q107, Q108, Q109]), "depth" : 0.94 * mm});
        }
        {
            var Q0;
            Q0=makeQuery(id+"F3.opExtrude","CAP_EDGE",EDGE,{"disambiguationData":[OSD([sQuery(id+"F1.wireOp",EDGE,"b0e0dee2-7c40-486c-a8eb-da6d1aebb478")])],"isStart":false});
            var Q1;
            Q1=makeQuery(id+"F3.opExtrude","CAP_EDGE",EDGE,{"disambiguationData":[OSD([sQuery(id+"F1.wireOp",EDGE,"04816a61-eb0e-4346-90f7-c6d7124d8b43")])],"isStart":false});
            var Q2;
            Q2=makeQuery(id+"F3.opExtrude","CAP_EDGE",EDGE,{"disambiguationData":[OSD([sQuery(id+"F1.wireOp",EDGE,"80e09545-e805-4756-afb3-e908e0697b95")])],"isStart":false});
            var Q3;
            Q3=makeQuery(id+"F3.opExtrude","CAP_EDGE",EDGE,{"disambiguationData":[OSD([sQuery(id+"F1.wireOp",EDGE,"0a267213-7c40-419e-a7d2-6af8714e5f45")])],"isStart":false});
            var Q4;
            Q4=makeQuery(id+"F3.opExtrude","CAP_EDGE",EDGE,{"disambiguationData":[OSD([sQuery(id+"F1.wireOp",EDGE,"4b321e91-a8a1-4189-b260-94da62a27512")])],"isStart":false});
            var Q5;
            Q5=makeQuery(id+"F3.opExtrude","CAP_EDGE",EDGE,{"disambiguationData":[OSD([sQuery(id+"F1.wireOp",EDGE,"7edd777e-64e0-4db0-8f52-2228dfb33078")])],"isStart":false});
            var Q6;
            Q6=makeQuery(id+"F3.opExtrude","CAP_EDGE",EDGE,{"disambiguationData":[OSD([sQuery(id+"F1.wireOp",EDGE,"5ca0945c-6bbc-48af-a93b-5625915023c8")])],"isStart":false});
            var Q7;
            Q7=makeQuery(id+"F3.opExtrude","CAP_EDGE",EDGE,{"disambiguationData":[OSD([sQuery(id+"F1.wireOp",EDGE,"bff61fca-36fd-4415-8d85-04465080573f")])],"isStart":false});
            var Q8;
            Q8=makeQuery(id+"F3.opExtrude","CAP_EDGE",EDGE,{"disambiguationData":[OSD([sQuery(id+"F1.wireOp",EDGE,"e07ccc40-30e0-4116-87f5-dd35409532ab")])],"isStart":false});
            var Q9;
            Q9=makeQuery(id+"F3.opExtrude","CAP_EDGE",EDGE,{"disambiguationData":[OSD([sQuery(id+"F1.wireOp",EDGE,"1916121b-87e3-42fd-bb47-9bf82f42e5d9")])],"isStart":false});
            var Q10;
            Q10=makeQuery(id+"F3.opExtrude","CAP_EDGE",EDGE,{"disambiguationData":[OSD([sQuery(id+"F1.wireOp",EDGE,"8f9b4e0b-b456-4ce4-89e9-5843fb71aecc")])],"isStart":false});
            var Q11;
            Q11=makeQuery(id+"F3.opExtrude","CAP_EDGE",EDGE,{"disambiguationData":[OSD([sQuery(id+"F1.wireOp",EDGE,"56acc55b-9546-466a-93d2-c752bbd7866e")])],"isStart":false});
            var Q12;
            Q12=makeQuery(id+"F3.opExtrude","CAP_EDGE",EDGE,{"disambiguationData":[OSD([sQuery(id+"F1.wireOp",EDGE,"e43c900f-e10d-4cac-8d11-2e5689b6b1d5")])],"isStart":false});
            var Q13;
            Q13=makeQuery(id+"F3.opExtrude","CAP_EDGE",EDGE,{"disambiguationData":[OSD([sQuery(id+"F1.wireOp",EDGE,"559fe54c-6345-47de-806c-53990a12e350")])],"isStart":false});
            var Q14;
            Q14=makeQuery(id+"F3.opExtrude","CAP_EDGE",EDGE,{"disambiguationData":[OSD([sQuery(id+"F1.wireOp",EDGE,"a9e5a808-2ef5-4392-9576-852277e467f2")])],"isStart":false});
            var Q15;
            Q15=makeQuery(id+"F3.opExtrude","CAP_EDGE",EDGE,{"disambiguationData":[OSD([sQuery(id+"F1.wireOp",EDGE,"20040cfe-7ec2-40a3-b60c-debe91aca25c")])],"isStart":false});
            var Q16;
            Q16=makeQuery(id+"F3.opExtrude","CAP_EDGE",EDGE,{"disambiguationData":[OSD([sQuery(id+"F1.wireOp",EDGE,"25661483-70bc-4f2a-a87d-232d989049ff")])],"isStart":false});
            var Q17;
            Q17=makeQuery(id+"F3.opExtrude","CAP_EDGE",EDGE,{"disambiguationData":[OSD([sQuery(id+"F1.wireOp",EDGE,"IQYQTx4D-fJSk-LKtq-i42c-D6EXXIsjCsXz")])],"isStart":false});
            var Q18;
            Q18=makeQuery(id+"F3.opExtrude","CAP_EDGE",EDGE,{"disambiguationData":[OSD([sQuery(id+"F1.wireOp",EDGE,"6d958931-b70a-49d3-b1e5-2076e474eeb5")])],"isStart":false});
            var Q19;
            Q19=makeQuery(id+"F3.opExtrude","CAP_EDGE",EDGE,{"disambiguationData":[OSD([sQuery(id+"F1.wireOp",EDGE,"afb39670-50f2-49b1-be07-c2a09c23c589")])],"isStart":false});
            var Q20;
            Q20=makeQuery(id+"F3.opExtrude","CAP_EDGE",EDGE,{"disambiguationData":[OSD([sQuery(id+"F1.wireOp",EDGE,"4a20ea9f-2355-40fc-b659-074ddab8549f")])],"isStart":false});
            var Q21;
            Q21=makeQuery(id+"F3.opExtrude","CAP_EDGE",EDGE,{"disambiguationData":[OSD([sQuery(id+"F1.wireOp",EDGE,"0e15a808-7b14-42e8-9234-6df6935beb3e")])],"isStart":false});
            var Q22;
            Q22=makeQuery(id+"F3.opExtrude","CAP_EDGE",EDGE,{"disambiguationData":[OSD([sQuery(id+"F1.wireOp",EDGE,"48f5f1cd-c210-4d07-9456-369a695a64fd")])],"isStart":false});
            var Q23;
            Q23=makeQuery(id+"F3.opExtrude","CAP_EDGE",EDGE,{"disambiguationData":[OSD([sQuery(id+"F1.wireOp",EDGE,"d94de641-2fb7-41d4-b6e0-2e3dc5f59612")])],"isStart":false});
            var Q24;
            Q24=makeQuery(id+"F3.opExtrude","CAP_EDGE",EDGE,{"disambiguationData":[OSD([sQuery(id+"F0.wireOp",EDGE,"E0")])],"isStart":false});
            var Q25;
            Q25=makeQuery(id+"F3.opExtrude","CAP_EDGE",EDGE,{"disambiguationData":[OSD([sQuery(id+"F1.wireOp",EDGE,"7d899a2b-71f5-44ce-8364-893d38b0a961")])],"isStart":false});
            var Q26;
            Q26=makeQuery(id+"F3.opExtrude","CAP_EDGE",EDGE,{"disambiguationData":[OSD([sQuery(id+"F1.wireOp",EDGE,"9fa9e04d-5760-4a40-aeb6-4168d89a4eef")])],"isStart":false});
            var Q27;
            Q27=makeQuery(id+"F3.opExtrude","CAP_EDGE",EDGE,{"disambiguationData":[OSD([sQuery(id+"F1.wireOp",EDGE,"410c9de7-6207-49c7-be39-20c216db85bf")])],"isStart":false});
            var Q28;
            Q28=makeQuery(id+"F3.opExtrude","CAP_EDGE",EDGE,{"disambiguationData":[OSD([sQuery(id+"F1.wireOp",EDGE,"ab028f4d-2498-446a-b172-ba7fe3d4d79f")])],"isStart":false});
            var Q29;
            Q29=makeQuery(id+"F3.opExtrude","CAP_EDGE",EDGE,{"disambiguationData":[OSD([sQuery(id+"F1.wireOp",EDGE,"a645aaaa-f54e-411b-9215-a7927be1f780")])],"isStart":false});
            var Q30;
            Q30=makeQuery(id+"F3.opExtrude","CAP_EDGE",EDGE,{"disambiguationData":[OSD([sQuery(id+"F1.wireOp",EDGE,"9dde0bd0-4224-40f4-94b5-97fa1c3db23d")])],"isStart":false});
            var Q31;
            Q31=makeQuery(id+"F3.opExtrude","CAP_EDGE",EDGE,{"disambiguationData":[OSD([sQuery(id+"F1.wireOp",EDGE,"3b7f7286-30fc-4e50-92d2-53d9abb117fb")])],"isStart":false});
            var Q32;
            Q32=makeQuery(id+"F3.opExtrude","CAP_EDGE",EDGE,{"disambiguationData":[OSD([sQuery(id+"F1.wireOp",EDGE,"21019b6d-9225-4829-b8bd-877c992cc65f")])],"isStart":false});
            var Q33;
            Q33=makeQuery(id+"F3.opExtrude","CAP_EDGE",EDGE,{"disambiguationData":[OSD([sQuery(id+"F1.wireOp",EDGE,"d69b603a-0a3a-470c-87fb-5fe536fbcdfb")])],"isStart":false});
            var Q34;
            Q34=makeQuery(id+"F3.opExtrude","CAP_EDGE",EDGE,{"disambiguationData":[OSD([sQuery(id+"F1.wireOp",EDGE,"c8bbaf4e-987e-4e69-8a47-3c79a83e0c87")])],"isStart":false});
            var Q35;
            Q35=makeQuery(id+"F3.opExtrude","CAP_EDGE",EDGE,{"disambiguationData":[OSD([sQuery(id+"F1.wireOp",EDGE,"2c68a5cc-583a-4e21-8d00-f2716ba61d92")])],"isStart":false});
            var Q36;
            Q36=makeQuery(id+"F3.opExtrude","CAP_EDGE",EDGE,{"disambiguationData":[OSD([sQuery(id+"F1.wireOp",EDGE,"f4cf1d7a-71f4-429e-a2cf-aa9f5c4bf02f")])],"isStart":false});
            var Q37;
            Q37=makeQuery(id+"F3.opExtrude","CAP_EDGE",EDGE,{"disambiguationData":[OSD([sQuery(id+"F1.wireOp",EDGE,"1c02878d-3e23-409d-a322-f7ee412d3750")])],"isStart":false});
            var Q38;
            Q38=makeQuery(id+"F3.opExtrude","CAP_EDGE",EDGE,{"disambiguationData":[OSD([sQuery(id+"F1.wireOp",EDGE,"25866dd3-af03-4969-bc58-9b283e6d481b")])],"isStart":false});
            var Q39;
            Q39=makeQuery(id+"F3.opExtrude","CAP_EDGE",EDGE,{"disambiguationData":[OSD([sQuery(id+"F1.wireOp",EDGE,"05a9797e-15e3-4fd6-a2da-66079b940148")])],"isStart":false});
            var Q40;
            Q40=makeQuery(id+"F3.opExtrude","CAP_EDGE",EDGE,{"disambiguationData":[OSD([sQuery(id+"F1.wireOp",EDGE,"8f773712-27e5-4475-b0bc-b5b0b1b0142c")])],"isStart":false});
            var Q41;
            Q41=makeQuery(id+"F3.opExtrude","CAP_EDGE",EDGE,{"disambiguationData":[OSD([sQuery(id+"F1.wireOp",EDGE,"bc114b7d-a9ae-4e2b-965a-efcba974dd4e")])],"isStart":false});
            var Q42;
            Q42=makeQuery(id+"F3.opExtrude","CAP_EDGE",EDGE,{"disambiguationData":[OSD([sQuery(id+"F1.wireOp",EDGE,"c71889e1-eb4f-436c-9950-13deb293f1db")])],"isStart":false});
            var Q43;
            Q43=makeQuery(id+"F3.opExtrude","CAP_EDGE",EDGE,{"disambiguationData":[OSD([sQuery(id+"F1.wireOp",EDGE,"dc40b896-e991-42b1-9757-3a5ebb1f78ea")])],"isStart":false});
            var Q44;
            Q44=makeQuery(id+"F3.opExtrude","CAP_EDGE",EDGE,{"disambiguationData":[OSD([sQuery(id+"F1.wireOp",EDGE,"50d7f0cc-a3bc-44f1-927f-4ccd5fb9444e")])],"isStart":false});
            var Q45;
            Q45=makeQuery(id+"F3.opExtrude","CAP_EDGE",EDGE,{"disambiguationData":[OSD([sQuery(id+"F1.wireOp",EDGE,"407f0a36-e44a-4196-afc8-af34e5d263da")])],"isStart":false});
            var Q46;
            Q46=makeQuery(id+"F3.opExtrude","CAP_EDGE",EDGE,{"disambiguationData":[OSD([sQuery(id+"F1.wireOp",EDGE,"7f88ff2e-a912-4057-b699-7ce09ea38530")])],"isStart":false});
            var Q47;
            Q47=makeQuery(id+"F3.opExtrude","CAP_EDGE",EDGE,{"disambiguationData":[OSD([sQuery(id+"F1.wireOp",EDGE,"946e2664-ac89-45e9-bb45-cd7e8761c812")])],"isStart":false});
            var Q48;
            Q48=makeQuery(id+"F3.opExtrude","CAP_EDGE",EDGE,{"disambiguationData":[OSD([sQuery(id+"F1.wireOp",EDGE,"4e26d3ae-beb9-4c1a-93ba-002415f0acb0")])],"isStart":false});
            var Q49;
            Q49=makeQuery(id+"F3.opExtrude","CAP_EDGE",EDGE,{"disambiguationData":[OSD([sQuery(id+"F1.wireOp",EDGE,"47c9dda0-eb43-4ddc-b7b5-d2f01c861544")])],"isStart":false});
            var Q50;
            Q50=makeQuery(id+"F3.opExtrude","CAP_EDGE",EDGE,{"disambiguationData":[OSD([sQuery(id+"F1.wireOp",EDGE,"3106ccec-705c-4960-a74f-be933f157d40")])],"isStart":false});
            var Q51;
            Q51=makeQuery(id+"F3.opExtrude","CAP_EDGE",EDGE,{"disambiguationData":[OSD([sQuery(id+"F1.wireOp",EDGE,"b4ff40dc-20b4-4bd3-89fc-f102a9961f8c")])],"isStart":false});
            var Q52;
            Q52=makeQuery(id+"F3.opExtrude","CAP_EDGE",EDGE,{"disambiguationData":[OSD([sQuery(id+"F1.wireOp",EDGE,"bfb1065a-cab9-4898-b917-bb85fffde635")])],"isStart":false});
            var Q53;
            Q53=makeQuery(id+"F3.opExtrude","CAP_EDGE",EDGE,{"disambiguationData":[OSD([sQuery(id+"F1.wireOp",EDGE,"5daa7517-ec5d-4592-a1ac-977ff9070edf")])],"isStart":false});
            var Q54;
            Q54=makeQuery(id+"F3.opExtrude","CAP_EDGE",EDGE,{"disambiguationData":[OSD([sQuery(id+"F1.wireOp",EDGE,"53b61e4c-e748-4765-b0b8-36f6e8858f6d")])],"isStart":false});
            var Q55;
            Q55=makeQuery(id+"F3.opExtrude","CAP_EDGE",EDGE,{"disambiguationData":[OSD([sQuery(id+"F1.wireOp",EDGE,"2e7f4e81-c6df-418f-94df-d4b0b7ba906e")])],"isStart":false});
            var Q56;
            Q56=makeQuery(id+"F3.opExtrude","CAP_EDGE",EDGE,{"disambiguationData":[OSD([sQuery(id+"F1.wireOp",EDGE,"b71d4cb1-866b-4d81-a721-a0ad96be9b8b")])],"isStart":false});
            var Q57;
            Q57=makeQuery(id+"F3.opExtrude","CAP_EDGE",EDGE,{"disambiguationData":[OSD([sQuery(id+"F1.wireOp",EDGE,"6f771d5e-fdfe-4922-8dcd-cc699ffee86c")])],"isStart":false});
            var Q58;
            Q58=makeQuery(id+"F3.opExtrude","CAP_EDGE",EDGE,{"disambiguationData":[OSD([sQuery(id+"F1.wireOp",EDGE,"ce97bbf4-a538-4860-89d0-490cc9d6ba0e")])],"isStart":false});
            var Q59;
            Q59=makeQuery(id+"F3.opExtrude","CAP_EDGE",EDGE,{"disambiguationData":[OSD([sQuery(id+"F1.wireOp",EDGE,"c751a891-51ce-4e8d-9e0e-479f614fe617")])],"isStart":false});
            var Q60;
            Q60=makeQuery(id+"F3.opExtrude","CAP_EDGE",EDGE,{"disambiguationData":[OSD([sQuery(id+"F1.wireOp",EDGE,"55a967fc-cf59-4a71-bfac-7d7444c0d945")])],"isStart":false});
            var Q61;
            Q61=makeQuery(id+"F3.opExtrude","CAP_EDGE",EDGE,{"disambiguationData":[OSD([sQuery(id+"F1.wireOp",EDGE,"e3f8fca8-a1ae-4d0b-93d8-ef3dc832972e")])],"isStart":false});
            var Q62;
            Q62=makeQuery(id+"F3.opExtrude","CAP_EDGE",EDGE,{"disambiguationData":[OSD([sQuery(id+"F1.wireOp",EDGE,"d3ae8674-74f6-49cf-8c5c-0de1270b44e5")])],"isStart":false});
            var Q63;
            Q63=makeQuery(id+"F3.opExtrude","CAP_EDGE",EDGE,{"disambiguationData":[OSD([sQuery(id+"F1.wireOp",EDGE,"351b4d51-b6fd-40e4-8a24-322787a033b8")])],"isStart":false});
            var Q64;
            Q64=makeQuery(id+"F3.opExtrude","CAP_EDGE",EDGE,{"disambiguationData":[OSD([sQuery(id+"F1.wireOp",EDGE,"25d9cc1b-062b-4bb5-9ce4-53bc4fe40080")])],"isStart":false});
            var Q65;
            Q65=makeQuery(id+"F3.opExtrude","CAP_EDGE",EDGE,{"disambiguationData":[OSD([sQuery(id+"F1.wireOp",EDGE,"3b40a63c-9782-4902-8a86-c3139b9eb764")])],"isStart":false});
            var Q66;
            Q66=makeQuery(id+"F3.opExtrude","CAP_EDGE",EDGE,{"disambiguationData":[OSD([sQuery(id+"F1.wireOp",EDGE,"2cd982d5-0089-4635-972d-67435d39a214")])],"isStart":false});
            var Q67;
            Q67=makeQuery(id+"F3.opExtrude","CAP_EDGE",EDGE,{"disambiguationData":[OSD([sQuery(id+"F1.wireOp",EDGE,"2ee18cf7-4fb7-4b61-a3cf-e68d8f2852b4")])],"isStart":false});
            var Q68;
            Q68=makeQuery(id+"F3.opExtrude","CAP_EDGE",EDGE,{"disambiguationData":[OSD([sQuery(id+"F1.wireOp",EDGE,"ddde8b18-6fe0-4bc3-820a-1cbee6d39207")])],"isStart":false});
            var Q69;
            Q69=makeQuery(id+"F3.opExtrude","CAP_EDGE",EDGE,{"disambiguationData":[OSD([sQuery(id+"F1.wireOp",EDGE,"d1da2f99-7152-417c-86a7-0e482ec30a58")])],"isStart":false});
            var Q70;
            Q70=makeQuery(id+"F3.opExtrude","CAP_EDGE",EDGE,{"disambiguationData":[OSD([sQuery(id+"F1.wireOp",EDGE,"ba64a743-74b2-49ca-b953-3069a09bc900")])],"isStart":false});
            var Q71;
            Q71=makeQuery(id+"F3.opExtrude","CAP_EDGE",EDGE,{"disambiguationData":[OSD([sQuery(id+"F1.wireOp",EDGE,"5fa7571f-411c-4993-86c9-208f069f7377")])],"isStart":false});
            var Q72;
            Q72=makeQuery(id+"F3.opExtrude","CAP_EDGE",EDGE,{"disambiguationData":[OSD([sQuery(id+"F1.wireOp",EDGE,"7079bfff-28f3-4683-ae2e-cec7d5cb01cb")])],"isStart":false});
            var Q73;
            Q73=makeQuery(id+"F3.opExtrude","CAP_EDGE",EDGE,{"disambiguationData":[OSD([sQuery(id+"F1.wireOp",EDGE,"f7c1084b-d84e-4c82-aa00-e076926db26a")])],"isStart":false});
            var Q74;
            Q74=makeQuery(id+"F3.opExtrude","CAP_EDGE",EDGE,{"disambiguationData":[OSD([sQuery(id+"F1.wireOp",EDGE,"e37c8894-658f-4642-971c-f70e5ecd7af9")])],"isStart":false});
            var Q75;
            Q75=makeQuery(id+"F3.opExtrude","CAP_EDGE",EDGE,{"disambiguationData":[OSD([sQuery(id+"F1.wireOp",EDGE,"9eaee011-cf2f-4949-90a7-00d6302f023d")])],"isStart":false});
            var Q76;
            Q76=makeQuery(id+"F3.opExtrude","CAP_EDGE",EDGE,{"disambiguationData":[OSD([sQuery(id+"F1.wireOp",EDGE,"f6faf651-b7ee-4778-ad8d-2e4a8e9642f7")])],"isStart":false});
            var Q77;
            Q77=makeQuery(id+"F3.opExtrude","CAP_EDGE",EDGE,{"disambiguationData":[OSD([sQuery(id+"F1.wireOp",EDGE,"9d3ff30b-5d5f-465d-aec8-0f0612a3a9cd")])],"isStart":false});
            var Q78;
            Q78=makeQuery(id+"F3.opExtrude","CAP_EDGE",EDGE,{"disambiguationData":[OSD([sQuery(id+"F1.wireOp",EDGE,"61445ce6-51c2-4ac1-9eed-13ce467cc58e")])],"isStart":false});
            var Q79;
            Q79=makeQuery(id+"F3.opExtrude","CAP_EDGE",EDGE,{"disambiguationData":[OSD([sQuery(id+"F1.wireOp",EDGE,"7924a3fe-2feb-48c6-84bb-4c5bd13528d8")])],"isStart":false});
            var Q80;
            Q80=makeQuery(id+"F3.opExtrude","CAP_EDGE",EDGE,{"disambiguationData":[OSD([sQuery(id+"F1.wireOp",EDGE,"fc0269ad-6765-42d2-a3f1-cf348a22c25d")])],"isStart":false});
            var Q81;
            Q81=makeQuery(id+"F3.opExtrude","CAP_EDGE",EDGE,{"disambiguationData":[OSD([sQuery(id+"F1.wireOp",EDGE,"7d530aef-c8df-49cc-a853-35ad8e8a77fe")])],"isStart":false});
            var Q82;
            Q82=makeQuery(id+"F3.opExtrude","CAP_EDGE",EDGE,{"disambiguationData":[OSD([sQuery(id+"F1.wireOp",EDGE,"85043f60-7fef-43b8-ba61-ac2b7be8fe33")])],"isStart":false});
            var Q83;
            Q83=makeQuery(id+"F3.opExtrude","CAP_EDGE",EDGE,{"disambiguationData":[OSD([sQuery(id+"F1.wireOp",EDGE,"afdb87ec-d79a-45a9-a05c-717156bfb7cd")])],"isStart":false});
            var Q84;
            Q84=makeQuery(id+"F3.opExtrude","CAP_EDGE",EDGE,{"disambiguationData":[OSD([sQuery(id+"F1.wireOp",EDGE,"13c5ac6e-9f7b-46d0-b330-e33b265c37d4")])],"isStart":false});
            var Q85;
            Q85=makeQuery(id+"F3.opExtrude","CAP_EDGE",EDGE,{"disambiguationData":[OSD([sQuery(id+"F1.wireOp",EDGE,"cdf477c9-51f3-44c7-bcdf-c6a147e22681")])],"isStart":false});
            var Q86;
            Q86=makeQuery(id+"F3.opExtrude","CAP_EDGE",EDGE,{"disambiguationData":[OSD([sQuery(id+"F1.wireOp",EDGE,"7cfd9803-ecd4-4c70-86c0-bd39d4e26022")])],"isStart":false});
            var Q87;
            Q87=makeQuery(id+"F3.opExtrude","CAP_EDGE",EDGE,{"disambiguationData":[OSD([sQuery(id+"F1.wireOp",EDGE,"1b0e43d8-f7af-48e3-ac0b-2aa93e71bc35")])],"isStart":false});
            var Q88;
            Q88=makeQuery(id+"F3.opExtrude","CAP_EDGE",EDGE,{"disambiguationData":[OSD([sQuery(id+"F1.wireOp",EDGE,"126f70df-1a0d-451e-9d83-f86c9f88abc8")])],"isStart":false});
            var Q89;
            Q89=makeQuery(id+"F3.opExtrude","CAP_EDGE",EDGE,{"disambiguationData":[OSD([sQuery(id+"F1.wireOp",EDGE,"a09209f8-7044-4cf4-8aec-d30c1fa2ae95")])],"isStart":false});
            var Q90;
            Q90=makeQuery(id+"F3.opExtrude","CAP_FACE",FACE,{"disambiguationData":[OSD([sQuery(id+"F1.wireOp",EDGE,"84f1e03e-5a21-4721-94f0-bdbfdc29db09")])],"isStart":false});
            var Q91;
            Q91=makeQuery(id+"F3.opExtrude","CAP_EDGE",EDGE,{"disambiguationData":[OSD([sQuery(id+"F1.wireOp",EDGE,"84f1e03e-5a21-4721-94f0-bdbfdc29db09")])],"isStart":false});
            var Q92;
            Q92=makeQuery(id+"F3.opExtrude","CAP_EDGE",EDGE,{"disambiguationData":[OSD([sQuery(id+"F1.wireOp",EDGE,"a1965818-b970-4097-b521-540a1cb1f767")])],"isStart":false});
            var Q93;
            Q93=makeQuery(id+"F3.opExtrude","CAP_EDGE",EDGE,{"disambiguationData":[OSD([sQuery(id+"F1.wireOp",EDGE,"55cb77bc-91cc-4325-939e-488937f48d64")])],"isStart":false});
            var Q94;
            Q94=makeQuery(id+"F3.opExtrude","CAP_EDGE",EDGE,{"disambiguationData":[OSD([sQuery(id+"F1.wireOp",EDGE,"39267c74-a86e-4a0a-b377-4f9ec4585843")])],"isStart":false});
            var Q95;
            Q95=makeQuery(id+"F3.opExtrude","CAP_EDGE",EDGE,{"disambiguationData":[OSD([sQuery(id+"F1.wireOp",EDGE,"606e4ff4-c372-45cb-a36b-f10931f5497d")])],"isStart":false});
            var Q96;
            Q96=makeQuery(id+"F3.opExtrude","CAP_EDGE",EDGE,{"disambiguationData":[OSD([sQuery(id+"F1.wireOp",EDGE,"150f6f36-60db-42e5-89f4-495b7c08a796")])],"isStart":false});
            var Q97;
            Q97=makeQuery(id+"F3.opExtrude","CAP_EDGE",EDGE,{"disambiguationData":[OSD([sQuery(id+"F1.wireOp",EDGE,"8c1e2644-bb36-4412-ad06-52bd8adad983")])],"isStart":false});
            var Q98;
            Q98=makeQuery(id+"F3.opExtrude","CAP_EDGE",EDGE,{"disambiguationData":[OSD([sQuery(id+"F1.wireOp",EDGE,"5996a8f3-71d1-45d0-9633-99fc3c2019b6")])],"isStart":false});
            var Q99;
            Q99=makeQuery(id+"F3.opExtrude","CAP_EDGE",EDGE,{"disambiguationData":[OSD([sQuery(id+"F1.wireOp",EDGE,"a48a8bff-ce23-473c-b1c0-9448eced9b32")])],"isStart":false});
            var Q100;
            Q100=makeQuery(id+"F3.opExtrude","CAP_EDGE",EDGE,{"disambiguationData":[OSD([sQuery(id+"F1.wireOp",EDGE,"0434efe0-d554-483d-bd28-34a7d8d0b50f")])],"isStart":false});
            var Q101;
            Q101=makeQuery(id+"F3.opExtrude","CAP_EDGE",EDGE,{"disambiguationData":[OSD([sQuery(id+"F1.wireOp",EDGE,"40bdc2a5-2341-4f5c-a56b-06b630dfa9fc")])],"isStart":false});
            var Q102;
            Q102=makeQuery(id+"F3.opExtrude","CAP_EDGE",EDGE,{"disambiguationData":[OSD([sQuery(id+"F1.wireOp",EDGE,"2b311b18-58fd-43b0-ac47-cf94851b1c52")])],"isStart":false});
            var Q103;
            Q103=makeQuery(id+"F3.opExtrude","CAP_EDGE",EDGE,{"disambiguationData":[OSD([sQuery(id+"F1.wireOp",EDGE,"1a7c10c3-2d57-4d46-a384-873822354761")])],"isStart":false});
            var Q104;
            Q104=makeQuery(id+"F3.opExtrude","CAP_EDGE",EDGE,{"disambiguationData":[OSD([sQuery(id+"F1.wireOp",EDGE,"484d747a-906d-4482-9977-9e7a5c9f7520")])],"isStart":false});
            var Q105;
            Q105=makeQuery(id+"F3.opExtrude","CAP_EDGE",EDGE,{"disambiguationData":[OSD([sQuery(id+"F1.wireOp",EDGE,"187869be-c3a0-4a53-b3f3-32ef39bbe492")])],"isStart":false});
            var Q106;
            Q106=makeQuery(id+"F3.opExtrude","CAP_EDGE",EDGE,{"disambiguationData":[OSD([sQuery(id+"F1.wireOp",EDGE,"95b728b6-ea23-49c0-ab31-382de2099b98")])],"isStart":false});
            var Q107;
            Q107=makeQuery(id+"F3.opExtrude","CAP_EDGE",EDGE,{"disambiguationData":[OSD([sQuery(id+"F1.wireOp",EDGE,"722cfd06-0ee1-456e-8828-1f596be15dbe")])],"isStart":false});
            var Q108;
            Q108=makeQuery(id+"F3.opExtrude","CAP_EDGE",EDGE,{"disambiguationData":[OSD([sQuery(id+"F1.wireOp",EDGE,"5295e683-5c6e-4e8e-bbfe-81816525bda0")])],"isStart":false});
            var Q109;
            Q109=makeQuery(id+"F3.opExtrude","CAP_EDGE",EDGE,{"disambiguationData":[OSD([sQuery(id+"F1.wireOp",EDGE,"19382886-88d1-4d62-8e9d-aeeddef3f290")])],"isStart":false});
            var Q110;
            Q110=makeQuery(id+"F3.opExtrude","CAP_EDGE",EDGE,{"disambiguationData":[OSD([sQuery(id+"F1.wireOp",EDGE,"6e8f4bdd-71aa-42b2-a188-63b31c486d87")])],"isStart":false});
            fillet(context, id + "F4", {"entities" : qUnion([Q0, Q1, Q2, Q3, Q4, Q5, Q6, Q7, Q8, Q9, Q10, Q11, Q12, Q13, Q14, Q15, Q16, Q17, Q18, Q19, Q20, Q21, Q22, Q23, Q24, Q25, Q26, Q27, Q28, Q29, Q30, Q31, Q32, Q33, Q34, Q35, Q36, Q37, Q38, Q39, Q40, Q41, Q42, Q43, Q44, Q45, Q46, Q47, Q48, Q49, Q50, Q51, Q52, Q53, Q54, Q55, Q56, Q57, Q58, Q59, Q60, Q61, Q62, Q63, Q64, Q65, Q66, Q67, Q68, Q69, Q70, Q71, Q72, Q73, Q74, Q75, Q76, Q77, Q78, Q79, Q80, Q81, Q82, Q83, Q84, Q85, Q86, Q87, Q88, Q89, Q90, Q91, Q92, Q93, Q94, Q95, Q96, Q97, Q98, Q99, Q100, Q101, Q102, Q103, Q104, Q105, Q106, Q107, Q108, Q109, Q110]), "radius" : .6 * mm, "tangentPropagation" : true, "rho" : .3, "crossSection" : FilletCrossSection.CONIC, "allowEdgeOverflow" : false});
        }
        {
            var Q0;
            {var subQ1=sQuery(id+"F2.wireOp",EDGE,"wk7LG9wq-JaKf-7Txt-Pqvq-ZvWdc8VFdTcg.bottom");Q0=makeQuery(id+"F2.imprint","IMPRINT",FACE,{"disambiguationData":[TD([[makeQuery(id+"F2.imprint","IMPRINT",EDGE,{"derivedFrom":subQ1}),-1.0]])]});}
            var Q1;
            Q1=makeQuery(id+"F1.imprint","IMPRINT",FACE,{"disambiguationData":[TD([[makeQuery(id+"F1.imprint","IMPRINT",EDGE,{"derivedFrom":sQuery(id+"F1.wireOp",EDGE,"IQYQTx4D-fJSk-LKtq-i42c-D6EXXIsjCsXz")}),-1.0]])]});
            var Q2;
            {var subQ0=sQuery(id+"F1.wireOp",EDGE,"E5");Q2=makeQuery(id+"F1.imprint","IMPRINT",FACE,{"disambiguationData":[TD([[makeQuery(id+"F1.imprint","IMPRINT",EDGE,{"derivedFrom":subQ0}),-1.0]])]});}
            extrude(context, id + "F5", {"entities" : qUnion([Q0, Q1, Q2]), "oppositeDirection" : true, "depth" : 1.02 * mm});
        }
        {
            var Q0;
            Q0=makeQuery(id+"F3.opExtrude","SWEPT_BODY",BODY,{"disambiguationData":[OSD([sQuery(id+"F0.wireOp",EDGE,"E0")])]});
            deleteBodies(context, id + "F6", {"entities" : qUnion([Q0])});
        }
    });
